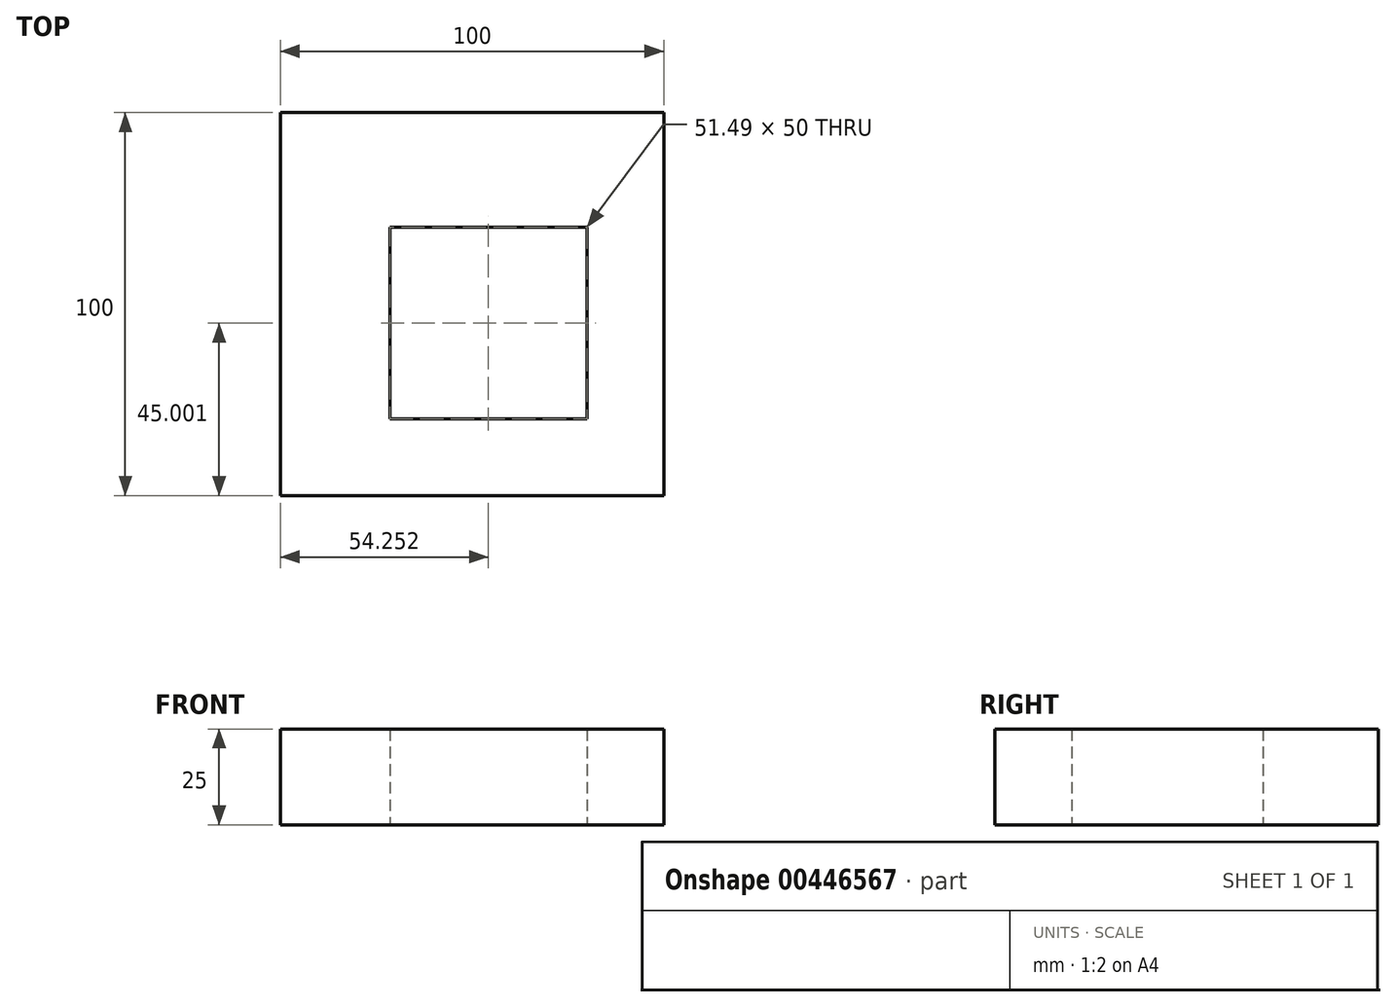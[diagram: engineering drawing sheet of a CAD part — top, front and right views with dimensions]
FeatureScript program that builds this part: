
annotation { "Feature Type Name" : "Feature", "Feature Type Description" : "" }
export const myFeature = defineFeature(function(context is Context, id is Id, definition is map)
    precondition{}
    {
        {
            var Q0;
            Q0=qCreatedBy(makeId("Top.planeOp"),FACE);
            var sketch = newSketch(context, id + "F0", { "sketchPlane" : qUnion([Q0])});
            skLineSegment(sketch, "E0.bottom", {"start": v(-68.15, -42.48) * mm, "end": v(31.85, -42.48) * mm});
            skLineSegment(sketch, "E0.top", {"start": v(-68.15, 57.52) * mm, "end": v(31.85, 57.52) * mm});
            skLineSegment(sketch, "E0.left", {"start": v(-68.15, -42.48) * mm, "end": v(-68.15, 57.52) * mm});
            skLineSegment(sketch, "E0.right", {"start": v(31.85, -42.48) * mm, "end": v(31.85, 57.52) * mm});
            skLineSegment(sketch, "E1.0", {"start": v(931.85, -42.48) * mm, "end": v(931.85, 57.52) * mm});
            skLineSegment(sketch, "E2.bottom", {"start": v(-39.64, -22.48) * mm, "end": v(11.85, -22.48) * mm});
            skLineSegment(sketch, "E2.top", {"start": v(-39.64, 27.52) * mm, "end": v(11.85, 27.52) * mm});
            skLineSegment(sketch, "E2.left", {"start": v(-39.64, -22.48) * mm, "end": v(-39.64, 27.52) * mm});
            skLineSegment(sketch, "E2.right", {"start": v(11.85, -22.48) * mm, "end": v(11.85, 27.52) * mm});
            skSolve(sketch);
        }
        {
            var Q0;
            Q0=makeQuery(id+"F0.imprint","IMPRINT",FACE,{"disambiguationData":[TD([[makeQuery(id+"F0.imprint","IMPRINT",EDGE,{"derivedFrom":sQuery(id+"F0.wireOp",EDGE,"E0.bottom")}),1.0]])]});
            extrude(context, id + "F1", {"entities" : qUnion([Q0]), "depth" : 25 * mm});
        }
    });
